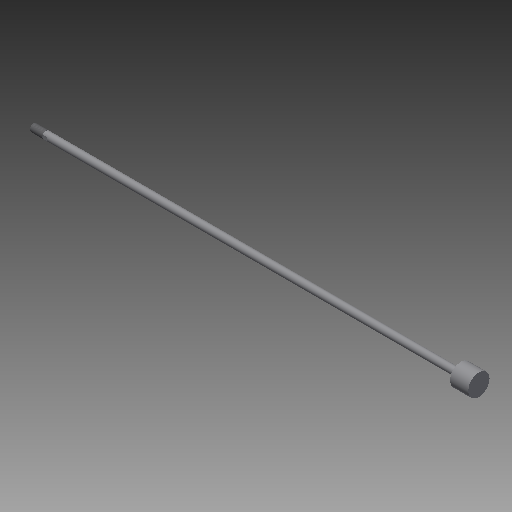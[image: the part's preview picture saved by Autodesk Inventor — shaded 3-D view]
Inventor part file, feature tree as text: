
AUTODESK INVENTOR PART (.ipt)
format: ipt  version: 2019 (Build 230136000, 136)  size: 160,256 bytes
history: native  units: in
note: dims shown in document units (in); Inventor stores cm internally (conversion verified against a paired STEP export)
features: other x112, sketch x3, revolve x2, thread x1, extrude x1
ambient origin geometry x8: Origin, YZ Plane, XZ Plane, XY Plane, X Axis, Y Axis, Z Axis, Center Point
bodies: Solid1 (feature_tree)
feature tree (119):
  revolve  "Revolution1"  Angle=360.0deg
  revolve  "Revolution2"  [1 undecoded]
  thread  "Thread1"  [1 undecoded]
  extrude  "Extrusion1"  [1 undecoded]
  other  "dia1_XY"
  other  "dia1_YZ"
  other  "dia1_ZX"
  other  "dia1_X"
  other  "dia1_Y"
  other  "dia1_Z"
  other  "dia1_Center"
  other  "dia12_XY"
  other  "dia12_YZ"
  other  "dia12_ZX"
  other  "dia12_X"
  other  "dia12_Y"
  other  "dia12_Z"
  other  "dia12_Center"
  other  "dia2_XY"
  other  "dia2_YZ"
  other  "dia2_ZX"
  other  "dia2_X"
  other  "dia2_Y"
  other  "dia2_Z"
  other  "dia2_Center"
  other  "dia22_XY"
  other  "dia22_YZ"
  other  "dia22_ZX"
  other  "dia22_X"
  other  "dia22_Y"
  other  "dia22_Z"
  other  "dia22_Center"
  other  "hh1_XY"
  other  "hh1_YZ"
  other  "hh1_ZX"
  other  "hh1_X"
  other  "hh1_Y"
  other  "hh1_Z"
  other  "hh1_Center"
  other  "hh2_XY"
  other  "hh2_YZ"
  other  "hh2_ZX"
  other  "hh2_X"
  other  "hh2_Y"
  other  "hh2_Z"
  other  "hh2_Center"
  other  "rl1_XY"
  other  "rl1_YZ"
  other  "rl1_ZX"
  other  "rl1_X"
  other  "rl1_Y"
  other  "rl1_Z"
  other  "rl1_Center"
  other  "rl2_XY"
  other  "rl2_YZ"
  other  "rl2_ZX"
  other  "rl2_X"
  other  "rl2_Y"
  other  "rl2_Z"
  other  "rl2_Center"
  other  "rod_cp_XY"
  other  "rod_cp_YZ"
  other  "rod_cp_ZX"
  other  "rod_cp_X"
  other  "rod_cp_Y"
  other  "rod_cp_Z"
  other  "rod_cp_Center"
  other  "thd1_XY"
  other  "thd1_YZ"
  other  "thd1_ZX"
  other  "thd1_X"
  other  "thd1_Y"
  other  "thd1_Z"
  other  "thd1_Center"
  other  "thd2_XY"
  other  "thd2_YZ"
  other  "thd2_ZX"
  other  "thd2_X"
  other  "thd2_Y"
  other  "thd2_Z"
  other  "thd2_Center"
  other  "to_rod_clevis_XY"
  other  "to_rod_clevis_YZ"
  other  "to_rod_clevis_ZX"
  other  "to_rod_clevis_X"
  other  "to_rod_clevis_Y"
  other  "to_rod_clevis_Z"
  other  "to_rod_clevis_Center"
  other  "wf1_XY"
  other  "wf1_YZ"
  other  "wf1_ZX"
  other  "wf1_X"
  other  "wf1_Y"
  other  "wf1_Z"
  other  "wf1_Center"
  other  "wf2_XY"
  other  "wf2_YZ"
  other  "wf2_ZX"
  other  "wf2_X"
  other  "wf2_Y"
  other  "wf2_Z"
  other  "wf2_Center"
  other  "wfw1_XY"
  other  "wfw1_YZ"
  other  "wfw1_ZX"
  other  "wfw1_X"
  other  "wfw1_Y"
  other  "wfw1_Z"
  other  "wfw1_Center"
  other  "wfw2_XY"
  other  "wfw2_YZ"
  other  "wfw2_ZX"
  other  "wfw2_X"
  other  "wfw2_Y"
  other  "wfw2_Z"
  other  "wfw2_Center"
  sketch  "Sketch_1"  dims[d0=360.0deg d1=360.0deg]
  sketch  "Sketch_3"  dims[d2=0.7203in d3=0.0in d4=0.25in d5=0.0in]
  sketch  "Sketch_10"  dims[d6=0.0in d7=0.0in d8=0.0in d9=0.0in d10=0.0in d11=0.0in d12=0.0in]
note: 3 required parameter values undecoded (feature->parameter linkage not recoverable at this tier; creation-order binding heuristic only, values carry confidence <= 0.55)